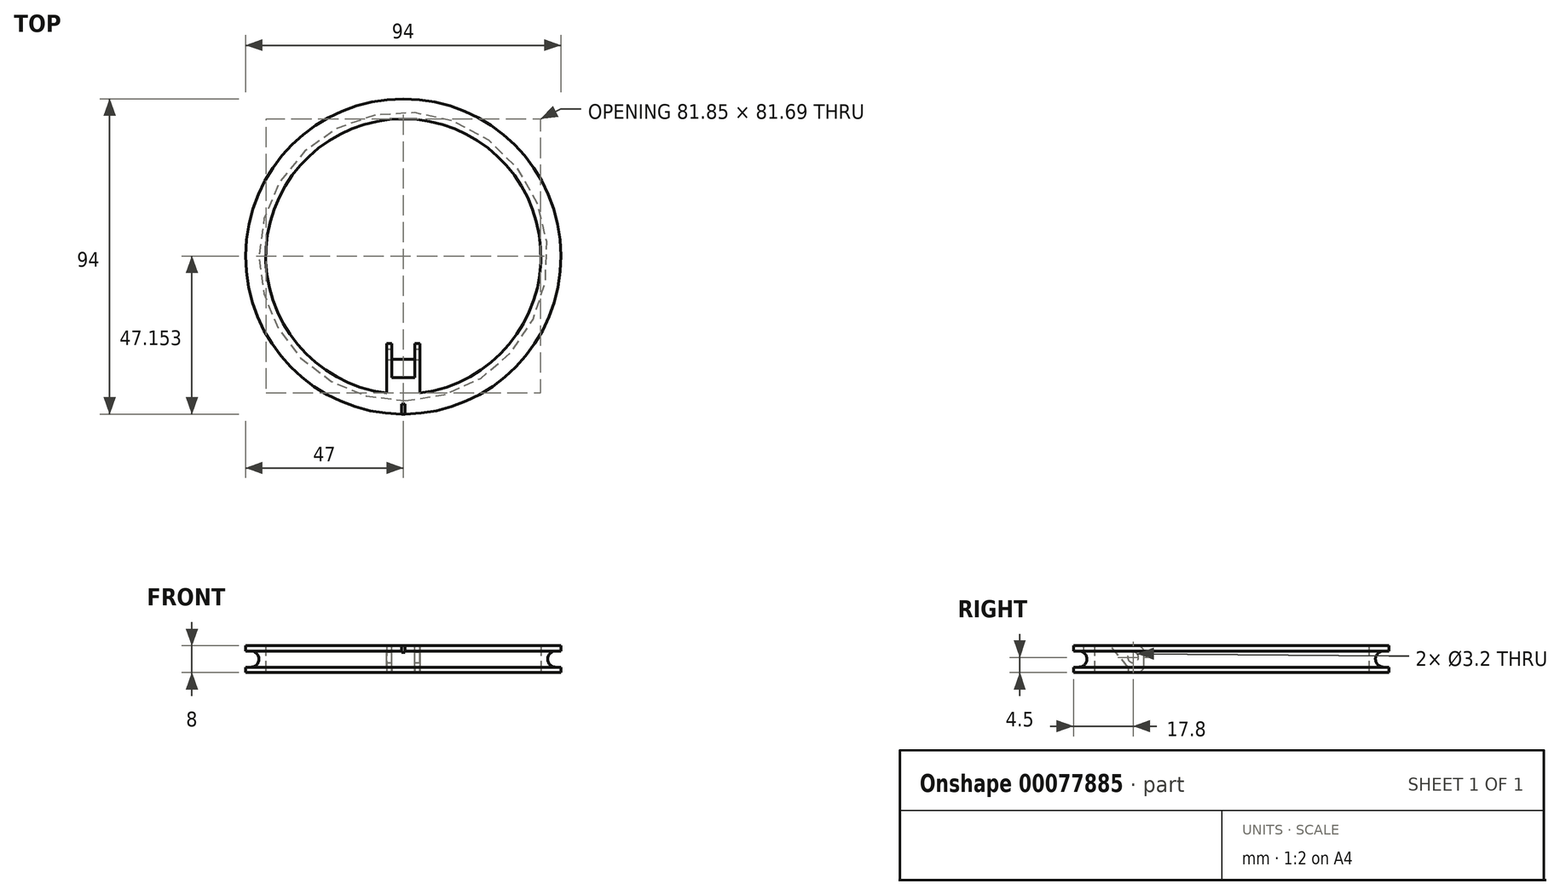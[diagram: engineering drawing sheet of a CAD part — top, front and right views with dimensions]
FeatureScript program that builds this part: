
annotation { "Feature Type Name" : "Feature", "Feature Type Description" : "" }
export const myFeature = defineFeature(function(context is Context, id is Id, definition is map)
    precondition{}
    {
        {
            var Q0;
            Q0=qCreatedBy(makeId("Front.planeOp"),FACE);
            var sketch = newSketch(context, id + "F0", { "sketchPlane" : qUnion([Q0])});
            skLineSegment(sketch, "E0.bottom", {"start": v(-47, 5) * mm, "end": v(-41, 5) * mm});
            skLineSegment(sketch, "E0.top", {"start": v(-47, -3) * mm, "end": v(-41, -3) * mm});
            skLineSegment(sketch, "E0.left", {"start": v(-47, 5) * mm, "end": v(-47, 3.4) * mm});
            skLineSegment(sketch, "E1", {"start": v(-47, 3.4) * mm, "end": v(-43, 3.4) * mm});
            skLineSegment(sketch, "E2", {"start": v(-43, 3.4) * mm, "end": v(-43, -1.4) * mm});
            skLineSegment(sketch, "E3", {"start": v(-43, -1.4) * mm, "end": v(-47, -1.4) * mm});
            skLineSegment(sketch, "E4", {"start": v(-41, -3) * mm, "end": v(-41, 5) * mm});
            skLineSegment(sketch, "E5.trimOffspring", {"start": v(-47, -1.4) * mm, "end": v(-47, -3) * mm});
            skLineSegment(sketch, "E6", {"start": v(0, -42.92) * mm, "end": v(0, 44.35) * mm, "construction": true});
            skSolve(sketch);
        }
        {
            var Q0;
            Q0=makeQuery(id+"F0.imprint","IMPRINT",FACE,{"disambiguationData":[TD([[makeQuery(id+"F0.imprint","IMPRINT",EDGE,{"derivedFrom":sQuery(id+"F0.wireOp",EDGE,"E0.bottom")}),-1.0]])]});
            var Q1;
            Q1=sQuery(id+"F0.wireOp",EDGE,"E6");
            revolve(context, id + "F1", {"entities" : qUnion([Q0]), "axis" : qUnion([Q1]), "revolveType" : RevolveType.FULL});
        }
        {
            var Q0;
            Q0=makeQuery(id+"F1.opRevolve","SWEPT_EDGE",EDGE,{"disambiguationData":[OSD([sQuery(id+"F0.wireOp",EDGE,"E1"),sQuery(id+"F0.wireOp",EDGE,"E2")])]});
            fillet(context, id + "F2", {"entities" : qUnion([Q0]), "radius" : 2.4 * mm, "tangentPropagation" : true, "allowEdgeOverflow" : false});
        }
        {
            var Q0;
            Q0=makeQuery(id+"F1.opRevolve","SWEPT_EDGE",EDGE,{"disambiguationData":[OSD([sQuery(id+"F0.wireOp",EDGE,"E2"),sQuery(id+"F0.wireOp",EDGE,"E3")])]});
            fillet(context, id + "F3", {"entities" : qUnion([Q0]), "radius" : 2.4 * mm, "tangentPropagation" : true, "allowEdgeOverflow" : false});
        }
        {
            var Q0;
            Q0=qCreatedBy(makeId("Front.planeOp"),FACE);
            cPlane(context, id + "F4", {"entities" : qUnion([Q0]), "cplaneType" : CPlaneType.OFFSET, "offset" : 26 * mm, "width" : 150 * mm, "height" : 150 * mm});
        }
        {
            var Q0;
            Q0=qCreatedBy(id+"F4.planeOp",FACE);
            var sketch = newSketch(context, id + "F5", { "sketchPlane" : qUnion([Q0])});
            skLineSegment(sketch, "E7", {"start": v(-5, 5) * mm, "end": v(5, 5) * mm});
            skLineSegment(sketch, "E8", {"start": v(5, 5) * mm, "end": v(5, -3) * mm});
            skLineSegment(sketch, "E9", {"start": v(-5, -3) * mm, "end": v(-5, 5) * mm});
            skLineSegment(sketch, "E10", {"start": v(0, 0) * mm, "end": v(0, 13.1) * mm, "construction": true});
            skLineSegment(sketch, "E11", {"start": v(-5, -3) * mm, "end": v(5, -3) * mm});
            skSolve(sketch);
        }
        {
            var Q0;
            Q0=makeQuery(id+"F5.imprint","IMPRINT",FACE,{"disambiguationData":[TD([[makeQuery(id+"F5.imprint","IMPRINT",EDGE,{"derivedFrom":sQuery(id+"F5.wireOp",EDGE,"E7")}),-1.0]])]});
            extrude(context, id + "F6", {"entities" : qUnion([Q0]), "operationType" : NewBodyOperationType.ADD, "endBound" : BoundingType.UP_TO_NEXT, "depth" : 25 * mm});
        }
        {
            var Q0;
            Q0=qCreatedBy(makeId("Right.planeOp"),FACE);
            var sketch = newSketch(context, id + "F7", { "sketchPlane" : qUnion([Q0])});
            skCircle(sketch, "E12", {"center": v(-29.2, 1.5) * mm, "radius": 1.6 * mm});
            skLineSegment(sketch, "E13", {"start": v(-36.4, 5.41) * mm, "end": v(-26, 5.41) * mm});
            skLineSegment(sketch, "E14", {"start": v(-26, 5.41) * mm, "end": v(-26, 3.04) * mm});
            skLineSegment(sketch, "E15", {"start": v(-26, -1.4) * mm, "end": v(-26, 3.04) * mm});
            skLineSegment(sketch, "E16", {"start": v(-37.4, -1.4) * mm, "end": v(-26, -1.4) * mm});
            skLineSegment(sketch, "E17", {"start": v(-26, -1.4) * mm, "end": v(-26, -3.3) * mm});
            skLineSegment(sketch, "E18", {"start": v(-26, -3.3) * mm, "end": v(-30.68, -3.3) * mm});
            skLineSegment(sketch, "E19", {"start": v(-30.68, -1.4) * mm, "end": v(-36.4, 5.41) * mm});
            skLineSegment(sketch, "E20", {"start": v(-30.68, -1.4) * mm, "end": v(-30.68, -3.3) * mm});
            skSolve(sketch);
        }
        {
            var Q0;
            Q0=makeQuery(id+"F7.imprint","IMPRINT",FACE,{"disambiguationData":[TD([[makeQuery(id+"F7.imprint","IMPRINT",EDGE,{"derivedFrom":sQuery(id+"F7.wireOp",EDGE,"E12")}),1.0]])]});
            var Q1;
            Q1=sQuery(id+"F7.wireOp",EDGE,"E12");
            extrude(context, id + "F8", {"entities" : qUnion([Q0]), "operationType" : NewBodyOperationType.REMOVE, "surfaceEntities" : qUnion([Q1]), "oppositeDirection" : true, "depth" : 10 * mm, "symmetric" : true});
        }
        {
            var Q0;
            Q0=makeQuery(id+"F7.imprint","IMPRINT",FACE,{"disambiguationData":[TD([[makeQuery(id+"F7.imprint","IMPRINT",EDGE,{"derivedFrom":sQuery(id+"F7.wireOp",EDGE,"E13")}),-1.0]])]});
            var Q1;
            {var subQ0=sQuery(id+"F7.wireOp",EDGE,"E17");Q1=makeQuery(id+"F7.imprint","IMPRINT",FACE,{"disambiguationData":[TD([[makeQuery(id+"F7.imprint","IMPRINT",EDGE,{"derivedFrom":subQ0}),-1.0]])]});}
            var Q2;
            {var subQ4=sQuery(id+"F7.wireOp",EDGE,"E15");Q2=makeQuery(id+"F7.imprint","IMPRINT",FACE,{"disambiguationData":[TD([[makeQuery(id+"F7.imprint","IMPRINT",EDGE,{"derivedFrom":subQ4}),1.0]])]});}
            var Q3;
            {var subQ0=sQuery(id+"F7.wireOp",EDGE,"F8J2WuBZ-XyZh-3OXJ-Wpbq-1Q87bSjDWZjz");var subQ1=sQuery(id+"F7.wireOp",EDGE,"E12");var subQ2=makeQuery(id+"F7.imprint","INTERSECT",VERTEX,{"disambiguationData":[OD(0.0)],"derivedFrom":[subQ1,subQ0]});Q3=makeQuery(id+"F7.imprint","IMPRINT",FACE,{"disambiguationData":[TD([[makeQuery(id+"F7.imprint","IMPRINT",EDGE,{"disambiguationData":[TD([[subQ2,1.0]])],"derivedFrom":subQ1}),1.0]])]});}
            extrude(context, id + "F9", {"entities" : qUnion([Q0, Q1, Q2, Q3]), "operationType" : NewBodyOperationType.REMOVE, "oppositeDirection" : true, "depth" : 6.8 * mm, "symmetric" : true});
        }
        {
            var Q0;
            {var subQ0=sQuery(id+"F5.wireOp",EDGE,"E9");var subQ1=sQuery(id+"F5.wireOp",EDGE,"E7");Q0=makeQuery(id+"F9.boolean.opBoolean","SPLIT",EDGE,{"disambiguationData":[TD([makeQuery(id+"F6.opExtrude","SWEPT_FACE",FACE,{"disambiguationData":[OSD([subQ0])]})])],"derivedFrom":makeQuery(id+"F6.opExtrude","CAP_EDGE",EDGE,{"disambiguationData":[OSD([subQ1])],"isStart":true})});}
            var Q1;
            {var subQ0=sQuery(id+"F5.wireOp",EDGE,"E8");var subQ1=sQuery(id+"F5.wireOp",EDGE,"E7");Q1=makeQuery(id+"F9.boolean.opBoolean","SPLIT",EDGE,{"disambiguationData":[TD([makeQuery(id+"F6.opExtrude","SWEPT_FACE",FACE,{"disambiguationData":[OSD([subQ0])]})])],"derivedFrom":makeQuery(id+"F6.opExtrude","CAP_EDGE",EDGE,{"disambiguationData":[OSD([subQ1])],"isStart":true})});}
            var Q2;
            Q2=makeQuery(id+"F6.opExtrude","CAP_EDGE",EDGE,{"disambiguationData":[OSD([sQuery(id+"F5.wireOp",EDGE,"E11")])],"isStart":true});
            var Q3;
            Q3=makeQuery(id+"F6.opExtrude","TWEAK_EDGE",EDGE,{"derivedFrom":[makeQuery(id+"F1.opRevolve","SWEPT_FACE",FACE,{"disambiguationData":[OSD([sQuery(id+"F0.wireOp",EDGE,"E4")])]}),makeQuery(id+"F5.imprint","IMPRINT",EDGE,{"derivedFrom":sQuery(id+"F5.wireOp",EDGE,"E9")})]});
            var Q4;
            Q4=makeQuery(id+"F6.opExtrude","TWEAK_EDGE",EDGE,{"derivedFrom":[makeQuery(id+"F1.opRevolve","SWEPT_FACE",FACE,{"disambiguationData":[OSD([sQuery(id+"F0.wireOp",EDGE,"E4")])]}),makeQuery(id+"F5.imprint","IMPRINT",EDGE,{"derivedFrom":sQuery(id+"F5.wireOp",EDGE,"E8")})]});
            fillet(context, id + "F10", {"entities" : qUnion([Q0, Q1, Q2, Q3, Q4]), "radius" : 2 * mm, "tangentPropagation" : true, "allowEdgeOverflow" : false});
        }
        {
            var Q0;
            Q0=qCreatedBy(makeId("Right.planeOp"),FACE);
            var sketch = newSketch(context, id + "F11", { "sketchPlane" : qUnion([Q0])});
            skLineSegment(sketch, "E21", {"start": v(-48, 1) * mm, "end": v(-48, 5) * mm});
            skLineSegment(sketch, "E22", {"start": v(-48, 5) * mm, "end": v(-44, 5) * mm});
            skLineSegment(sketch, "E23", {"start": v(-44, 5) * mm, "end": v(-44, 1) * mm});
            skLineSegment(sketch, "E24", {"start": v(-44, 1) * mm, "end": v(-48, 1) * mm});
            skSolve(sketch);
        }
        {
            var Q0;
            Q0 = qSketchRegion(id + "F11", true);
            extrude(context, id + "F12", {"entities" : qUnion([Q0]), "operationType" : NewBodyOperationType.REMOVE, "oppositeDirection" : true, "depth" : 1 * mm, "symmetric" : true});
        }
    });
